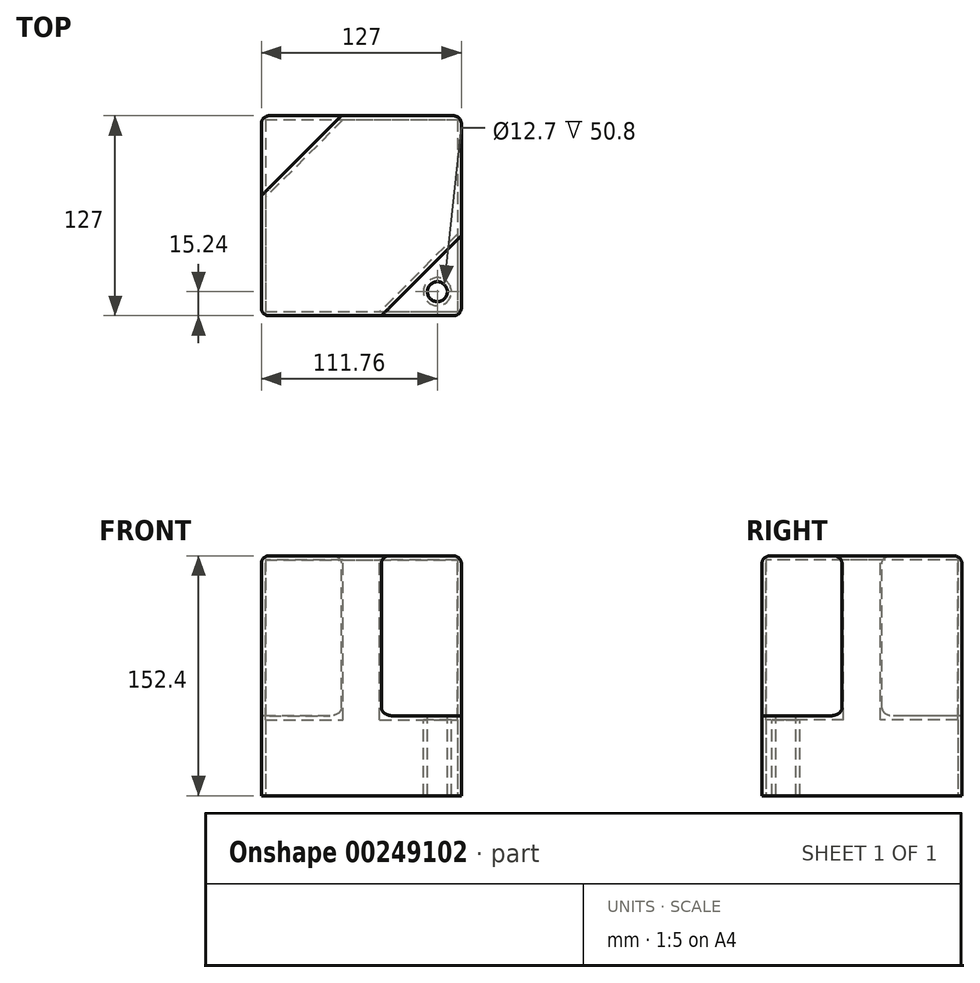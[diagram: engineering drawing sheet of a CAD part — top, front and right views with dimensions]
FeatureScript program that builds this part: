
annotation { "Feature Type Name" : "Feature", "Feature Type Description" : "" }
export const myFeature = defineFeature(function(context is Context, id is Id, definition is map)
    precondition{}
    {
        {
            var Q0;
            Q0=qCreatedBy(makeId("Top.planeOp"),FACE);
            var sketch = newSketch(context, id + "F0", { "sketchPlane" : qUnion([Q0])});
            skLineSegment(sketch, "E0.bottom", {"start": v(-63.5, 63.5) * mm, "end": v(63.5, 63.5) * mm});
            skLineSegment(sketch, "E0.top", {"start": v(-63.5, -63.5) * mm, "end": v(63.5, -63.5) * mm});
            skLineSegment(sketch, "E0.left", {"start": v(-63.5, 63.5) * mm, "end": v(-63.5, -63.5) * mm});
            skLineSegment(sketch, "E0.right", {"start": v(63.5, 63.5) * mm, "end": v(63.5, -63.5) * mm});
            skPoint(sketch, "E0.middle", {"position": v(0, 0) * mm});
            skSolve(sketch);
        }
        {
            var Q0;
            Q0=makeQuery(id+"F0.imprint","IMPRINT",FACE,{"disambiguationData":[TD([[makeQuery(id+"F0.imprint","IMPRINT",EDGE,{"derivedFrom":sQuery(id+"F0.wireOp",EDGE,"E0.bottom")}),-1.0]])]});
            extrude(context, id + "F1", {"entities" : qUnion([Q0]), "depth" : 152.4 * mm});
        }
        {
            var Q0;
            Q0=makeQuery(id+"F1.opExtrude","CAP_FACE",FACE,{"disambiguationData":[OSD([sQuery(id+"F0.wireOp",EDGE,"E0.bottom"),sQuery(id+"F0.wireOp",EDGE,"E0.top"),sQuery(id+"F0.wireOp",EDGE,"E0.left"),sQuery(id+"F0.wireOp",EDGE,"E0.right")])],"isStart":false});
            var sketch = newSketch(context, id + "F2", { "sketchPlane" : qUnion([Q0])});
            skLineSegment(sketch, "E1", {"start": v(-63.5, 63.5) * mm, "end": v(-12.7, 63.5) * mm});
            skLineSegment(sketch, "E2", {"start": v(-12.7, 63.5) * mm, "end": v(-63.5, 12.7) * mm});
            skLineSegment(sketch, "E3", {"start": v(-63.5, 12.7) * mm, "end": v(-63.5, 63.5) * mm});
            skLineSegment(sketch, "E4", {"start": v(-63.5, -63.5) * mm, "end": v(63.5, 63.5) * mm, "construction": true});
            skLineSegment(sketch, "E5", {"start": v(63.5, 63.5) * mm, "end": v(91.94, 91.51) * mm, "construction": true});
            skLineSegment(sketch, "E6.MirrorCS", {"start": v(12.7, -63.5) * mm, "end": v(63.5, -63.5) * mm});
            skLineSegment(sketch, "E7.MirrorCS", {"start": v(63.5, -63.5) * mm, "end": v(63.5, -12.7) * mm});
            skLineSegment(sketch, "E8.MirrorCS", {"start": v(63.5, -12.7) * mm, "end": v(12.7, -63.5) * mm});
            skSolve(sketch);
        }
        {
            var Q0;
            Q0=makeQuery(id+"F2.imprint","IMPRINT",FACE,{"disambiguationData":[TD([[makeQuery(id+"F2.imprint","IMPRINT",EDGE,{"derivedFrom":sQuery(id+"F2.wireOp",EDGE,"E1")}),-1.0]])]});
            var Q1;
            Q1=makeQuery(id+"F2.imprint","IMPRINT",FACE,{"disambiguationData":[TD([[makeQuery(id+"F2.imprint","IMPRINT",EDGE,{"derivedFrom":sQuery(id+"F2.wireOp",EDGE,"E6.MirrorCS")}),1.0]])]});
            extrude(context, id + "F3", {"entities" : qUnion([Q0, Q1]), "operationType" : NewBodyOperationType.REMOVE, "oppositeDirection" : true, "depth" : 101.6 * mm});
        }
        {
            var Q0;
            Q0=makeQuery(id+"F3.boolean.opBoolean","COPY",FACE,{"derivedFrom":makeQuery(id+"F3.opExtrude","CAP_FACE",FACE,{"disambiguationData":[OSD([sQuery(id+"F2.wireOp",EDGE,"E6.MirrorCS"),sQuery(id+"F2.wireOp",EDGE,"E7.MirrorCS"),sQuery(id+"F2.wireOp",EDGE,"E8.MirrorCS")])],"isStart":false})});
            var sketch = newSketch(context, id + "F4", { "sketchPlane" : qUnion([Q0])});
            skCircle(sketch, "E9", {"center": v(48.26, -48.26) * mm, "radius": 6.35 * mm});
            skLineSegment(sketch, "E10", {"start": v(0, 0) * mm, "end": v(-63.04, -63.82) * mm, "construction": true});
            skCircle(sketch, "E11.MirrorC", {"center": v(-48.85, 47.66) * mm, "radius": 6.35 * mm});
            skSolve(sketch);
        }
        {
            var Q0;
            Q0=makeQuery(id+"F4.imprint","IMPRINT",FACE,{"disambiguationData":[TD([[makeQuery(id+"F4.imprint","IMPRINT",EDGE,{"derivedFrom":sQuery(id+"F4.wireOp",EDGE,"E11.MirrorC")}),-1.0]])]});
            var Q1;
            Q1=makeQuery(id+"F4.imprint","IMPRINT",FACE,{"disambiguationData":[TD([[makeQuery(id+"F4.imprint","IMPRINT",EDGE,{"derivedFrom":sQuery(id+"F4.wireOp",EDGE,"E9")}),1.0]])]});
            extrude(context, id + "F5", {"entities" : qUnion([Q0, Q1]), "operationType" : NewBodyOperationType.REMOVE, "oppositeDirection" : true, "depth" : 203.2 * mm});
        }
        {
            var Q0;
            Q0=makeQuery(id+"F1.opExtrude","CAP_FACE",FACE,{"disambiguationData":[OSD([sQuery(id+"F0.wireOp",EDGE,"E0.bottom"),sQuery(id+"F0.wireOp",EDGE,"E0.top"),sQuery(id+"F0.wireOp",EDGE,"E0.left"),sQuery(id+"F0.wireOp",EDGE,"E0.right")])],"isStart":true});
            shell(context, id + "F6", {"entities" : qUnion([Q0]), "thickness" : 2.54 * mm});
        }
        {
            var Q0;
            Q0=makeQuery(id+"F3.boolean.opBoolean","COPY",EDGE,{"derivedFrom":makeQuery(id+"F3.opExtrude","CAP_EDGE",EDGE,{"disambiguationData":[OSD([sQuery(id+"F2.wireOp",EDGE,"E2")])],"isStart":true})});
            var Q1;
            Q1=makeQuery(id+"F3.boolean.opBoolean","COPY",EDGE,{"derivedFrom":makeQuery(id+"F3.opExtrude","CAP_EDGE",EDGE,{"disambiguationData":[OSD([sQuery(id+"F2.wireOp",EDGE,"E2")])],"isStart":false})});
            var Q2;
            Q2=makeQuery(id+"F3.boolean.opBoolean","COPY",EDGE,{"derivedFrom":makeQuery(id+"F3.opExtrude","CAP_EDGE",EDGE,{"disambiguationData":[OSD([sQuery(id+"F2.wireOp",EDGE,"E1")])],"isStart":false})});
            var Q3;
            Q3=makeQuery(id+"F1.opExtrude","CAP_EDGE",EDGE,{"disambiguationData":[OSD([sQuery(id+"F0.wireOp",EDGE,"E0.bottom")])],"isStart":false});
            var Q4;
            Q4=makeQuery(id+"F1.opExtrude","SWEPT_EDGE",EDGE,{"disambiguationData":[OSD([sQuery(id+"F0.wireOp",EDGE,"E0.bottom"),sQuery(id+"F0.wireOp",EDGE,"E0.right")])]});
            var Q5;
            Q5=makeQuery(id+"F1.opExtrude","CAP_EDGE",EDGE,{"disambiguationData":[OSD([sQuery(id+"F0.wireOp",EDGE,"E0.right")])],"isStart":false});
            var Q6;
            Q6=makeQuery(id+"F3.boolean.opBoolean","COPY",EDGE,{"derivedFrom":makeQuery(id+"F3.opExtrude","CAP_EDGE",EDGE,{"disambiguationData":[OSD([sQuery(id+"F2.wireOp",EDGE,"E8.MirrorCS")])],"isStart":true})});
            var Q7;
            Q7=makeQuery(id+"F3.boolean.opBoolean","COPY",EDGE,{"derivedFrom":makeQuery(id+"F3.opExtrude","SWEPT_EDGE",EDGE,{"disambiguationData":[OSD([sQuery(id+"F0.wireOp",EDGE,"E0.right"),sQuery(id+"F2.wireOp",EDGE,"E7.MirrorCS"),sQuery(id+"F2.wireOp",EDGE,"E8.MirrorCS")])]})});
            var Q8;
            Q8=makeQuery(id+"F3.boolean.opBoolean","COPY",EDGE,{"derivedFrom":makeQuery(id+"F3.opExtrude","CAP_EDGE",EDGE,{"disambiguationData":[OSD([sQuery(id+"F2.wireOp",EDGE,"E7.MirrorCS")])],"isStart":false})});
            var Q9;
            Q9=makeQuery(id+"F3.boolean.opBoolean","COPY",EDGE,{"derivedFrom":makeQuery(id+"F3.opExtrude","CAP_EDGE",EDGE,{"disambiguationData":[OSD([sQuery(id+"F2.wireOp",EDGE,"E6.MirrorCS")])],"isStart":false})});
            var Q10;
            Q10=makeQuery(id+"F1.opExtrude","CAP_EDGE",EDGE,{"disambiguationData":[OSD([sQuery(id+"F0.wireOp",EDGE,"E0.top")])],"isStart":false});
            var Q11;
            Q11=makeQuery(id+"F1.opExtrude","CAP_EDGE",EDGE,{"disambiguationData":[OSD([sQuery(id+"F0.wireOp",EDGE,"E0.left")])],"isStart":false});
            var Q12;
            Q12=makeQuery(id+"F1.opExtrude","SWEPT_EDGE",EDGE,{"disambiguationData":[OSD([sQuery(id+"F0.wireOp",EDGE,"E0.top"),sQuery(id+"F0.wireOp",EDGE,"E0.left")])]});
            var Q13;
            Q13=makeQuery(id+"F3.boolean.opBoolean","COPY",EDGE,{"derivedFrom":makeQuery(id+"F3.opExtrude","CAP_EDGE",EDGE,{"disambiguationData":[OSD([sQuery(id+"F2.wireOp",EDGE,"E3")])],"isStart":false})});
            var Q14;
            Q14=makeQuery(id+"F1.opExtrude","SWEPT_EDGE",EDGE,{"disambiguationData":[OSD([sQuery(id+"F0.wireOp",EDGE,"E0.bottom"),sQuery(id+"F0.wireOp",EDGE,"E0.left")])]});
            var Q15;
            Q15=makeQuery(id+"F1.opExtrude","SWEPT_EDGE",EDGE,{"disambiguationData":[OSD([sQuery(id+"F0.wireOp",EDGE,"E0.top"),sQuery(id+"F0.wireOp",EDGE,"E0.right")])]});
            var Q16;
            Q16=makeQuery(id+"F3.boolean.opBoolean","COPY",EDGE,{"derivedFrom":makeQuery(id+"F3.opExtrude","SWEPT_EDGE",EDGE,{"disambiguationData":[OSD([sQuery(id+"F0.wireOp",EDGE,"E0.top"),sQuery(id+"F2.wireOp",EDGE,"E6.MirrorCS"),sQuery(id+"F2.wireOp",EDGE,"E8.MirrorCS")])]})});
            var Q17;
            Q17=makeQuery(id+"F3.boolean.opBoolean","COPY",EDGE,{"derivedFrom":makeQuery(id+"F3.opExtrude","CAP_EDGE",EDGE,{"disambiguationData":[OSD([sQuery(id+"F2.wireOp",EDGE,"E8.MirrorCS")])],"isStart":false})});
            fillet(context, id + "F7", {"entities" : qUnion([Q0, Q1, Q2, Q3, Q4, Q5, Q6, Q7, Q8, Q9, Q10, Q11, Q12, Q13, Q14, Q15, Q16, Q17]), "radius" : 5.08 * mm, "tangentPropagation" : true, "allowEdgeOverflow" : false});
        }
    });
